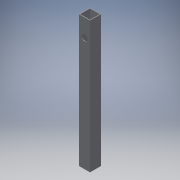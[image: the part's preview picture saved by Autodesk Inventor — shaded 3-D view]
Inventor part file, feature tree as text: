
AUTODESK INVENTOR PART (.ipt)
format: ipt  version: 2019.3 (Build 233278000, 278)  size: 123,904 bytes
history: native  units: mm
features: reference x7, extrude x4, sketch x4, other x3
ambient origin geometry x8: Origin, YZ Plane, XZ Plane, XY Plane, X Axis, Y Axis, Z Axis, Center Point
bodies: Solid1 (feature_tree)
feature tree (18):
  extrude  "Extrusion1"  Depth=300.0mm
  extrude  "Extrusion2"  Depth=22.225mm
  extrude  "Extrusion3"  Depth=25.4mm TaperAngle=0.0deg
  extrude  "Extrusion4"  Depth=25.4mm
  sketch  "Sketch1"  dims[d0=50.0mm d1=300.0mm]
  reference  "Reference1"
  reference  "Reference2"
  reference  "Reference3"
  sketch  "Sketch2"  dims[d2=25.4mm d3=0.0mm d4=22.225mm]
  reference  "Reference4"
  reference  "Reference5"
  sketch  "Sketch3"  dims[d5=1.5875mm d6=25.4mm d7=0.0mm]
  reference  "Reference6"
  reference  "Reference7"
  sketch  "Sketch4"  dims[d8=15.0mm d9=12.7mm d10=10.0mm d11=25.4mm d12=0.0mm d13=9.0mm d14=0.0mm d15=0.0mm]
  parser-record x1  (decoder bookkeeping rows leaked as tree rows — omitted from the tree; the rows remain in map.json)
  other  "Assembly.iam"
  other  "VerticalBar:1"
note: 1 file-system path scrubbed to <path> (originals preserved in map.json)
